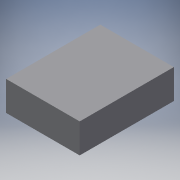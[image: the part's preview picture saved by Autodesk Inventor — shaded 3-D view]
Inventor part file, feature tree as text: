
AUTODESK INVENTOR PART (.ipt)
format: ipt  version: 2019 (Build 230136000, 136)  size: 86,528 bytes
history: native  units: in
note: dims shown in document units (in); Inventor stores cm internally (conversion verified against a paired STEP export)
features: extrude x1, sketch x1
ambient origin geometry x8: Origin, YZ Plane, XZ Plane, XY Plane, X Axis, Y Axis, Z Axis, Center Point
bodies: Solid1 (feature_tree)
feature tree (2):
  extrude  "Extrusion1"  Depth=3.2in
  sketch  "Sketch1"  dims[d0=2.5in d1=3.2in d2=1.0in d3=0.0in]
